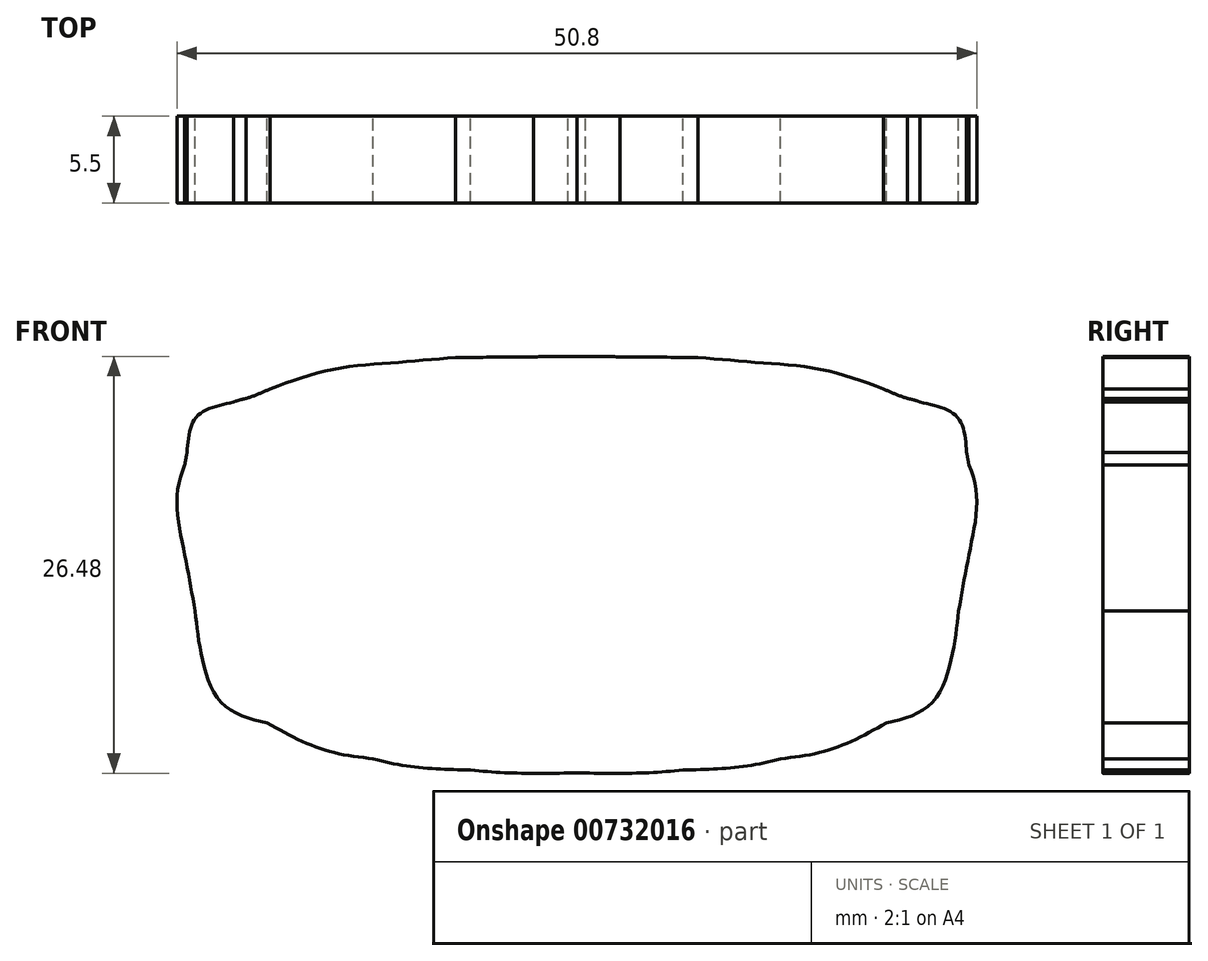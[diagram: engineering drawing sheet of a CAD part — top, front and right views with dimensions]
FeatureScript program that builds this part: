
annotation { "Feature Type Name" : "Feature", "Feature Type Description" : "" }
export const myFeature = defineFeature(function(context is Context, id is Id, definition is map)
    precondition{}
    {
        {
            var Q0;
            Q0=qCreatedBy(makeId("Front.planeOp"),FACE);
            var sketch = newSketch(context, id + "F0", { "sketchPlane" : qUnion([Q0])});
            skFitSpline(sketch, "E0", {"points": [v(0.55, -13.22) * mm, v(-5.68, -13.04) * mm, v(-12.04, -12.54) * mm, v(-17.9, -10.24) * mm]});
            skFitSpline(sketch, "E1", {"points": [v(-17.9, -10.24) * mm, v(-20.65, -9.04) * mm, v(-22.43, -6.39) * mm, v(-23.28, -3.58) * mm]});
            skFitSpline(sketch, "E2", {"points": [v(-23.28, -3.58) * mm, v(-24.47, -0.16) * mm, v(-25.17, 3.53) * mm, v(-24.76, 7.14) * mm]});
            skFitSpline(sketch, "E3", {"points": [v(-24.76, 7.14) * mm, v(-24.09, 9.48) * mm, v(-21.53, 10.42) * mm, v(-19.48, 11.18) * mm]});
            skFitSpline(sketch, "E4", {"points": [v(-19.48, 11.18) * mm, v(-15.66, 12.39) * mm, v(-11.66, 12.85) * mm, v(-7.69, 13.19) * mm]});
            skFitSpline(sketch, "E5", {"points": [v(-7.69, 13.19) * mm, v(-6.54, 13.18) * mm, v(-4.47, 13.22) * mm, v(-2.75, 13.22) * mm]});
            skFitSpline(sketch, "E6", {"points": [v(-2.75, 13.22) * mm, v(0.12, 13.24) * mm, v(2.99, 13.06) * mm, v(5.84, 12.73) * mm]});
            skFitSpline(sketch, "E7", {"points": [v(5.84, 12.73) * mm, v(7.23, 12.59) * mm, v(8.58, 12.49) * mm, v(10.04, 12.3) * mm]});
            skFitSpline(sketch, "E8", {"points": [v(10.04, 12.3) * mm, v(12.1, 12.25) * mm, v(14.12, 11.64) * mm, v(16.16, 11.35) * mm]});
            skFitSpline(sketch, "E9", {"points": [v(16.16, 11.35) * mm, v(18.86, 10.75) * mm, v(21.87, 10.32) * mm, v(23.91, 8.3) * mm]});
            skFitSpline(sketch, "E10", {"points": [v(23.91, 8.3) * mm, v(25.35, 4.76) * mm, v(24.93, 0.75) * mm, v(24.25, -2.92) * mm]});
            skFitSpline(sketch, "E11", {"points": [v(24.25, -2.92) * mm, v(23.83, -5.8) * mm, v(22.49, -8.83) * mm, v(19.66, -10.03) * mm]});
            skFitSpline(sketch, "E12", {"points": [v(19.66, -10.03) * mm, v(15.95, -11.77) * mm, v(11.83, -12.42) * mm, v(7.8, -12.9) * mm]});
            skFitSpline(sketch, "E13", {"points": [v(7.8, -12.9) * mm, v(5.39, -13.15) * mm, v(2.97, -13.23) * mm, v(0.55, -13.22) * mm]});
            skSolve(sketch);
        }
        {
            var Q0;
            Q0=qSketchRegion(id+"F0",true);
            extrude(context, id + "F1", {"entities" : qUnion([Q0]), "depth" : 5.5 * mm, "offsetDistance" : 25 * mm});
        }
        {
            var Q0;
            Q0=makeQuery(id+"F1.opExtrude","SWEPT_BODY",BODY,{"disambiguationData":[OSD([sQuery(id+"F0.wireOp",EDGE,"E0"),sQuery(id+"F0.wireOp",EDGE,"E1"),sQuery(id+"F0.wireOp",EDGE,"E2"),sQuery(id+"F0.wireOp",EDGE,"E3"),sQuery(id+"F0.wireOp",EDGE,"E4"),sQuery(id+"F0.wireOp",EDGE,"E5"),sQuery(id+"F0.wireOp",EDGE,"E6"),sQuery(id+"F0.wireOp",EDGE,"E7"),sQuery(id+"F0.wireOp",EDGE,"E8"),sQuery(id+"F0.wireOp",EDGE,"E9"),sQuery(id+"F0.wireOp",EDGE,"E10"),sQuery(id+"F0.wireOp",EDGE,"E11"),sQuery(id+"F0.wireOp",EDGE,"E12"),sQuery(id+"F0.wireOp",EDGE,"E13")])]});
            var Q1;
            Q1=qCreatedBy(makeId("Right.planeOp"),FACE);
            mirror(context, id + "F2", {"operationType" : NewBodyOperationType.ADD, "entities" : qUnion([Q0]), "mirrorPlane" : qUnion([Q1])});
        }
    });
